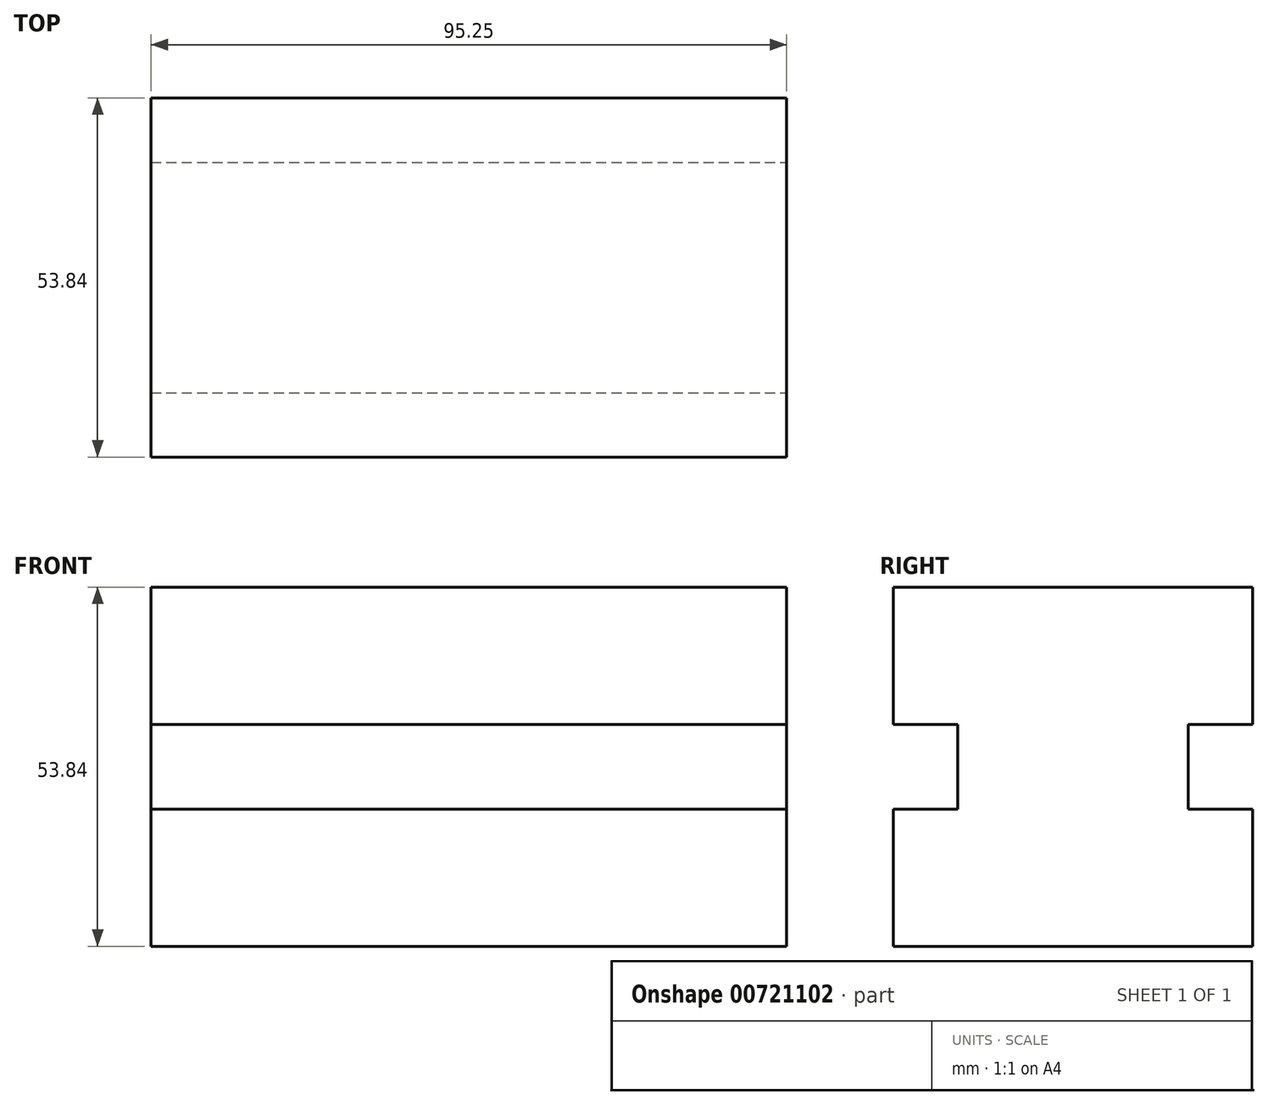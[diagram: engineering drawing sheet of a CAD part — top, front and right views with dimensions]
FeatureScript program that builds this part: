
annotation { "Feature Type Name" : "Feature", "Feature Type Description" : "" }
export const myFeature = defineFeature(function(context is Context, id is Id, definition is map)
    precondition{}
    {
        {
            var Q0;
            Q0=qCreatedBy(makeId("Right.planeOp"),FACE);
            var sketch = newSketch(context, id + "F0", { "sketchPlane" : qUnion([Q0])});
            skLineSegment(sketch, "E0.bottom", {"start": v(26.92, 26.92) * mm, "end": v(-26.92, 26.92) * mm});
            skLineSegment(sketch, "E0.top", {"start": v(26.92, -26.92) * mm, "end": v(-26.92, -26.92) * mm});
            skLineSegment(sketch, "E0.left", {"start": v(26.92, 26.92) * mm, "end": v(26.92, 6.35) * mm});
            skLineSegment(sketch, "E0.right", {"start": v(-26.92, 26.92) * mm, "end": v(-26.92, 6.35) * mm});
            skPoint(sketch, "E0.middle", {"position": v(0, 0) * mm});
            skLineSegment(sketch, "E1.bottom", {"start": v(-26.92, -6.35) * mm, "end": v(-17.27, -6.35) * mm});
            skLineSegment(sketch, "E1.top", {"start": v(-26.92, 6.35) * mm, "end": v(-17.27, 6.35) * mm});
            skLineSegment(sketch, "E1.right", {"start": v(-17.27, -6.35) * mm, "end": v(-17.27, 6.35) * mm});
            skLineSegment(sketch, "E2", {"start": v(0, 37) * mm, "end": v(0, -55.35) * mm, "construction": true});
            skPoint(sketch, "E2.startSnap0", {"position": v(0, 26.92) * mm});
            skLineSegment(sketch, "E3.MirrorCS", {"start": v(26.92, 6.35) * mm, "end": v(17.27, 6.35) * mm});
            skLineSegment(sketch, "E4.MirrorCS", {"start": v(17.27, -6.35) * mm, "end": v(17.27, 6.35) * mm});
            skLineSegment(sketch, "E5.MirrorCS", {"start": v(26.92, -6.35) * mm, "end": v(17.27, -6.35) * mm});
            skLineSegment(sketch, "E6.trimOffspring", {"start": v(-26.92, -6.35) * mm, "end": v(-26.92, -26.92) * mm});
            skLineSegment(sketch, "E7.trimOffspring", {"start": v(26.92, -6.35) * mm, "end": v(26.92, -26.92) * mm});
            skSolve(sketch);
        }
        {
            var Q0;
            Q0=makeQuery(id+"F0.imprint","IMPRINT",FACE,{"disambiguationData":[TD([[makeQuery(id+"F0.imprint","IMPRINT",EDGE,{"derivedFrom":sQuery(id+"F0.wireOp",EDGE,"E0.bottom")}),1.0]])]});
            extrude(context, id + "F1", {"entities" : qUnion([Q0]), "oppositeDirection" : true, "depth" : 95.25 * mm, "offsetDistance" : 25.4 * mm});
        }
    });
